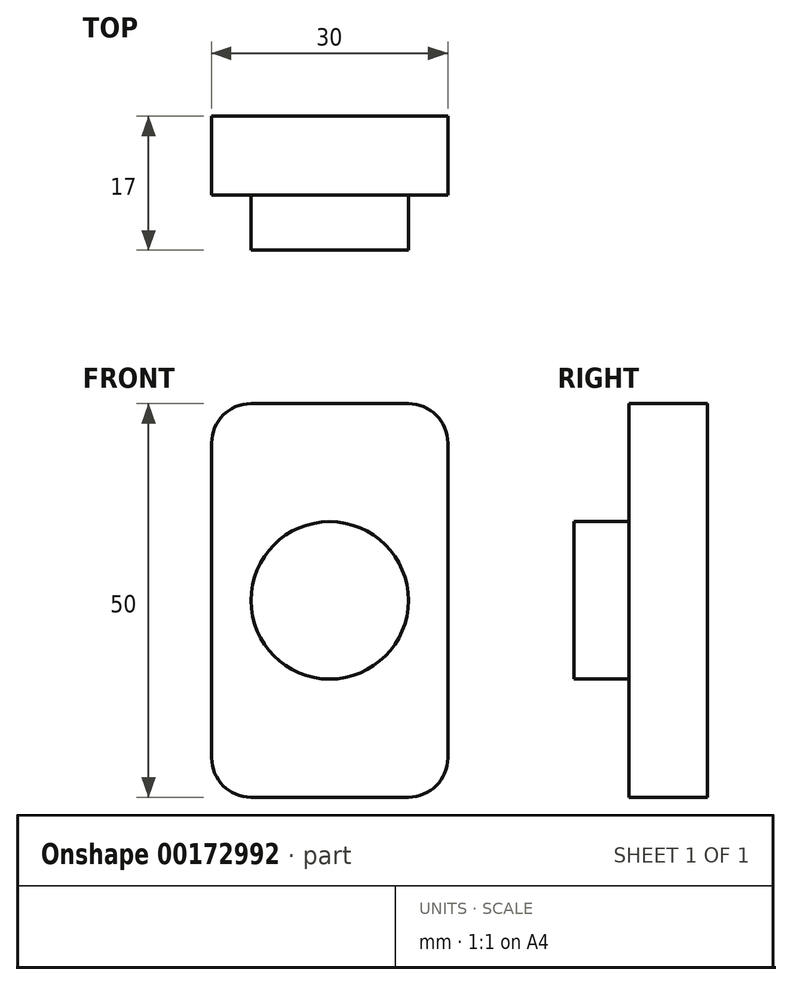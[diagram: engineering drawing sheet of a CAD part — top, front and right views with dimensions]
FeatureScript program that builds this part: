
annotation { "Feature Type Name" : "Feature", "Feature Type Description" : "" }
export const myFeature = defineFeature(function(context is Context, id is Id, definition is map)
    precondition{}
    {
        {
            var Q0;
            Q0=qCreatedBy(makeId("Front.planeOp"),FACE);
            var sketch = newSketch(context, id + "F0", { "sketchPlane" : qUnion([Q0])});
            skLineSegment(sketch, "E0.bottom", {"start": v(-15, -25) * mm, "end": v(15, -25) * mm});
            skLineSegment(sketch, "E0.top", {"start": v(-15, 25) * mm, "end": v(15, 25) * mm});
            skLineSegment(sketch, "E0.left", {"start": v(-15, -25) * mm, "end": v(-15, 25) * mm});
            skLineSegment(sketch, "E0.right", {"start": v(15, -25) * mm, "end": v(15, 25) * mm});
            skPoint(sketch, "E0.middle", {"position": v(0, 0) * mm});
            skSolve(sketch);
        }
        {
            var Q0;
            Q0=makeQuery(id+"F0.imprint","IMPRINT",FACE,{"disambiguationData":[TD([[makeQuery(id+"F0.imprint","IMPRINT",EDGE,{"derivedFrom":sQuery(id+"F0.wireOp",EDGE,"E0.bottom")}),1.0]])]});
            extrude(context, id + "F1", {"entities" : qUnion([Q0]), "oppositeDirection" : true, "depth" : 10 * mm});
        }
        {
            var Q0;
            Q0=makeQuery(id+"F1.opExtrude","CAP_FACE",FACE,{"disambiguationData":[OSD([sQuery(id+"F0.wireOp",EDGE,"E0.bottom"),sQuery(id+"F0.wireOp",EDGE,"E0.top"),sQuery(id+"F0.wireOp",EDGE,"E0.left"),sQuery(id+"F0.wireOp",EDGE,"E0.right")])],"isStart":true});
            var sketch = newSketch(context, id + "F2", { "sketchPlane" : qUnion([Q0])});
            skCircle(sketch, "E1", {"center": v(0, 0) * mm, "radius": 10 * mm});
            skSolve(sketch);
        }
        {
            var Q0;
            Q0=makeQuery(id+"F2.imprint","IMPRINT",FACE,{"disambiguationData":[TD([[makeQuery(id+"F2.imprint","IMPRINT",EDGE,{"derivedFrom":sQuery(id+"F2.wireOp",EDGE,"E1")}),1.0]])]});
            extrude(context, id + "F3", {"entities" : qUnion([Q0]), "operationType" : NewBodyOperationType.ADD, "depth" : 7 * mm});
        }
        {
            var Q0;
            Q0=makeQuery(id+"F1.opExtrude","SWEPT_EDGE",EDGE,{"disambiguationData":[OSD([sQuery(id+"F0.wireOp",EDGE,"E0.top"),sQuery(id+"F0.wireOp",EDGE,"E0.right")])]});
            fillet(context, id + "F4", {"entities" : qUnion([Q0]), "radius" : 5 * mm, "tangentPropagation" : true, "allowEdgeOverflow" : false});
        }
        {
            var Q0;
            Q0=makeQuery(id+"F1.opExtrude","SWEPT_EDGE",EDGE,{"disambiguationData":[OSD([sQuery(id+"F0.wireOp",EDGE,"E0.top"),sQuery(id+"F0.wireOp",EDGE,"E0.left")])]});
            fillet(context, id + "F5", {"entities" : qUnion([Q0]), "radius" : 5 * mm, "tangentPropagation" : true, "allowEdgeOverflow" : false});
        }
        {
            var Q0;
            Q0=makeQuery(id+"F1.opExtrude","SWEPT_EDGE",EDGE,{"disambiguationData":[OSD([sQuery(id+"F0.wireOp",EDGE,"E0.bottom"),sQuery(id+"F0.wireOp",EDGE,"E0.right")])]});
            fillet(context, id + "F6", {"entities" : qUnion([Q0]), "radius" : 5 * mm, "tangentPropagation" : true, "allowEdgeOverflow" : false});
        }
        {
            var Q0;
            Q0=makeQuery(id+"F1.opExtrude","SWEPT_EDGE",EDGE,{"disambiguationData":[OSD([sQuery(id+"F0.wireOp",EDGE,"E0.bottom"),sQuery(id+"F0.wireOp",EDGE,"E0.left")])]});
            fillet(context, id + "F7", {"entities" : qUnion([Q0]), "radius" : 5 * mm, "tangentPropagation" : true, "allowEdgeOverflow" : false});
        }
    });
